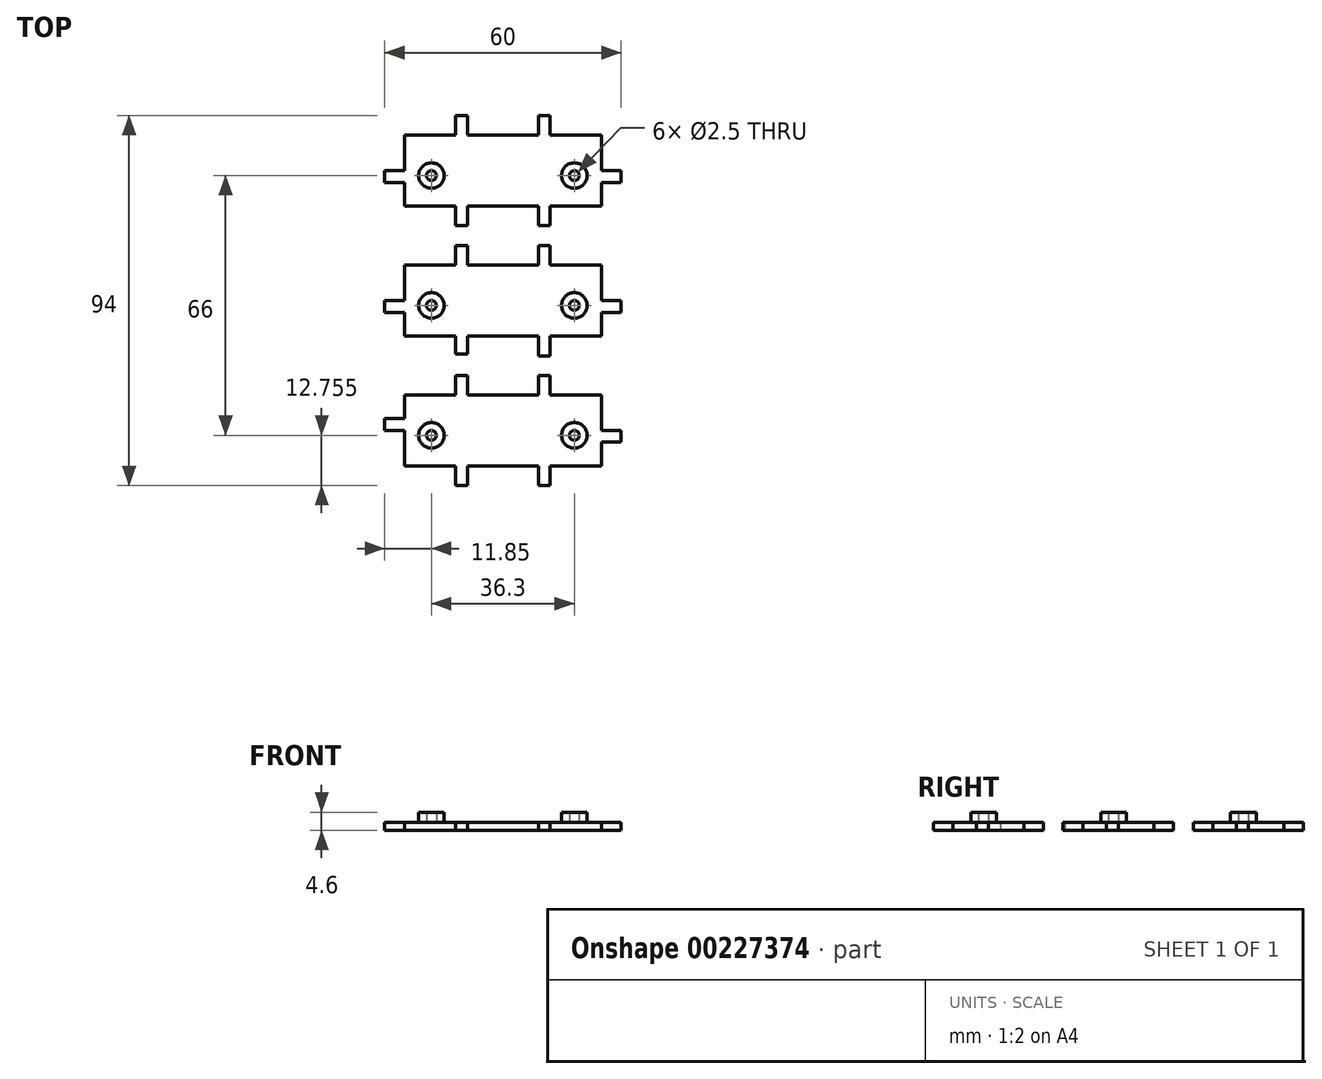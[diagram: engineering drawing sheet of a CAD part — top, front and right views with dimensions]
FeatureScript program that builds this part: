
annotation { "Feature Type Name" : "Feature", "Feature Type Description" : "" }
export const myFeature = defineFeature(function(context is Context, id is Id, definition is map)
    precondition{}
    {
        {
            var Q0;
            Q0=qCreatedBy(makeId("Top.planeOp"),FACE);
            var sketch = newSketch(context, id + "F0", { "sketchPlane" : qUnion([Q0])});
            skLineSegment(sketch, "E0.bottom", {"start": v(-14.26, 31.33) * mm, "end": v(35.74, 31.33) * mm});
            skLineSegment(sketch, "E0.top", {"start": v(-14.26, 13.33) * mm, "end": v(35.74, 13.33) * mm});
            skLineSegment(sketch, "E0.left", {"start": v(-14.26, 31.33) * mm, "end": v(-14.26, 13.33) * mm});
            skLineSegment(sketch, "E0.right", {"start": v(35.74, 31.33) * mm, "end": v(35.74, 13.33) * mm});
            skLineSegment(sketch, "E1.bottom", {"start": v(-14.26, -1.67) * mm, "end": v(35.74, -1.67) * mm});
            skLineSegment(sketch, "E1.top", {"start": v(-14.26, -19.67) * mm, "end": v(35.74, -19.67) * mm});
            skLineSegment(sketch, "E1.left", {"start": v(-14.26, -1.67) * mm, "end": v(-14.26, -19.67) * mm});
            skLineSegment(sketch, "E1.right", {"start": v(35.74, -1.67) * mm, "end": v(35.74, -19.67) * mm});
            skLineSegment(sketch, "E2.bottom", {"start": v(-14.26, -34.67) * mm, "end": v(35.74, -34.67) * mm});
            skLineSegment(sketch, "E2.top", {"start": v(-14.26, -52.67) * mm, "end": v(35.74, -52.67) * mm});
            skLineSegment(sketch, "E2.left", {"start": v(-14.26, -34.67) * mm, "end": v(-14.26, -52.67) * mm});
            skLineSegment(sketch, "E2.right", {"start": v(35.74, -34.67) * mm, "end": v(35.74, -52.67) * mm});
            skLineSegment(sketch, "E3.bottom", {"start": v(-1.26, 31.33) * mm, "end": v(1.74, 31.33) * mm});
            skLineSegment(sketch, "E3.top", {"start": v(-1.26, 36.33) * mm, "end": v(1.74, 36.33) * mm});
            skLineSegment(sketch, "E3.left", {"start": v(-1.26, 31.33) * mm, "end": v(-1.26, 36.33) * mm});
            skLineSegment(sketch, "E3.right", {"start": v(1.74, 31.33) * mm, "end": v(1.74, 36.33) * mm});
            skLineSegment(sketch, "E4.bottom", {"start": v(19.74, 36.33) * mm, "end": v(22.74, 36.33) * mm});
            skLineSegment(sketch, "E4.top", {"start": v(19.74, 31.33) * mm, "end": v(22.74, 31.33) * mm});
            skLineSegment(sketch, "E4.left", {"start": v(19.74, 36.33) * mm, "end": v(19.74, 31.33) * mm});
            skLineSegment(sketch, "E4.right", {"start": v(22.74, 36.33) * mm, "end": v(22.74, 31.33) * mm});
            skPoint(sketch, "E5.firstSnap0", {"position": v(-1.26, 33.83) * mm});
            skLineSegment(sketch, "E5.bottom", {"start": v(-1.26, 13.33) * mm, "end": v(1.74, 13.33) * mm});
            skLineSegment(sketch, "E5.top", {"start": v(-1.26, 8.33) * mm, "end": v(1.74, 8.33) * mm});
            skLineSegment(sketch, "E5.left", {"start": v(-1.26, 13.33) * mm, "end": v(-1.26, 8.33) * mm});
            skLineSegment(sketch, "E5.right", {"start": v(1.74, 13.33) * mm, "end": v(1.74, 8.33) * mm});
            skLineSegment(sketch, "E6.bottom", {"start": v(19.74, 13.33) * mm, "end": v(22.74, 13.33) * mm});
            skLineSegment(sketch, "E6.top", {"start": v(19.74, 8.33) * mm, "end": v(22.74, 8.33) * mm});
            skLineSegment(sketch, "E6.left", {"start": v(19.74, 13.33) * mm, "end": v(19.74, 8.33) * mm});
            skLineSegment(sketch, "E6.right", {"start": v(22.74, 13.33) * mm, "end": v(22.74, 8.33) * mm});
            skLineSegment(sketch, "E7.bottom", {"start": v(-1.26, -1.67) * mm, "end": v(1.74, -1.67) * mm});
            skLineSegment(sketch, "E7.top", {"start": v(-1.26, 3.33) * mm, "end": v(1.74, 3.33) * mm});
            skLineSegment(sketch, "E7.left", {"start": v(-1.26, -1.67) * mm, "end": v(-1.26, 3.33) * mm});
            skLineSegment(sketch, "E7.right", {"start": v(1.74, -1.67) * mm, "end": v(1.74, 3.33) * mm});
            skLineSegment(sketch, "E8.bottom", {"start": v(19.74, 3.33) * mm, "end": v(22.74, 3.33) * mm});
            skLineSegment(sketch, "E8.top", {"start": v(19.74, -1.67) * mm, "end": v(22.74, -1.67) * mm});
            skLineSegment(sketch, "E8.left", {"start": v(19.74, 3.33) * mm, "end": v(19.74, -1.67) * mm});
            skLineSegment(sketch, "E8.right", {"start": v(22.74, 3.33) * mm, "end": v(22.74, -1.67) * mm});
            skLineSegment(sketch, "E9.bottom", {"start": v(-1.26, -19.67) * mm, "end": v(1.74, -19.67) * mm});
            skLineSegment(sketch, "E9.top", {"start": v(-1.26, -24.3) * mm, "end": v(1.74, -24.3) * mm});
            skLineSegment(sketch, "E9.left", {"start": v(-1.26, -19.67) * mm, "end": v(-1.26, -24.3) * mm});
            skLineSegment(sketch, "E9.right", {"start": v(1.74, -19.67) * mm, "end": v(1.74, -24.3) * mm});
            skLineSegment(sketch, "E10.bottom", {"start": v(19.74, -19.67) * mm, "end": v(22.74, -19.67) * mm});
            skLineSegment(sketch, "E10.top", {"start": v(19.74, -24.78) * mm, "end": v(22.74, -24.78) * mm});
            skLineSegment(sketch, "E10.left", {"start": v(19.74, -19.67) * mm, "end": v(19.74, -24.78) * mm});
            skLineSegment(sketch, "E10.right", {"start": v(22.74, -19.67) * mm, "end": v(22.74, -24.78) * mm});
            skLineSegment(sketch, "E11.bottom", {"start": v(-1.26, -29.67) * mm, "end": v(1.74, -29.67) * mm});
            skLineSegment(sketch, "E11.top", {"start": v(-1.26, -34.67) * mm, "end": v(1.74, -34.67) * mm});
            skLineSegment(sketch, "E11.left", {"start": v(-1.26, -29.67) * mm, "end": v(-1.26, -34.67) * mm});
            skLineSegment(sketch, "E11.right", {"start": v(1.74, -29.67) * mm, "end": v(1.74, -34.67) * mm});
            skLineSegment(sketch, "E12.bottom", {"start": v(19.74, -29.67) * mm, "end": v(22.74, -29.67) * mm});
            skLineSegment(sketch, "E12.top", {"start": v(19.74, -34.67) * mm, "end": v(22.74, -34.67) * mm});
            skLineSegment(sketch, "E12.left", {"start": v(19.74, -29.67) * mm, "end": v(19.74, -34.67) * mm});
            skLineSegment(sketch, "E12.right", {"start": v(22.74, -29.67) * mm, "end": v(22.74, -34.67) * mm});
            skLineSegment(sketch, "E13.bottom", {"start": v(-1.26, -52.67) * mm, "end": v(1.74, -52.67) * mm});
            skLineSegment(sketch, "E13.top", {"start": v(-1.26, -57.67) * mm, "end": v(1.74, -57.67) * mm});
            skLineSegment(sketch, "E13.left", {"start": v(-1.26, -52.67) * mm, "end": v(-1.26, -57.67) * mm});
            skLineSegment(sketch, "E13.right", {"start": v(1.74, -52.67) * mm, "end": v(1.74, -57.67) * mm});
            skLineSegment(sketch, "E14.bottom", {"start": v(19.74, -52.67) * mm, "end": v(22.74, -52.67) * mm});
            skLineSegment(sketch, "E14.top", {"start": v(19.74, -57.67) * mm, "end": v(22.74, -57.67) * mm});
            skLineSegment(sketch, "E14.left", {"start": v(19.74, -52.67) * mm, "end": v(19.74, -57.67) * mm});
            skLineSegment(sketch, "E14.right", {"start": v(22.74, -52.67) * mm, "end": v(22.74, -57.67) * mm});
            skLineSegment(sketch, "E15.bottom", {"start": v(-14.26, 22.33) * mm, "end": v(-19.26, 22.33) * mm});
            skLineSegment(sketch, "E15.top", {"start": v(-14.26, 19.33) * mm, "end": v(-19.26, 19.33) * mm});
            skLineSegment(sketch, "E15.left", {"start": v(-14.26, 22.33) * mm, "end": v(-14.26, 19.33) * mm});
            skLineSegment(sketch, "E15.right", {"start": v(-19.26, 22.33) * mm, "end": v(-19.26, 19.33) * mm});
            skLineSegment(sketch, "E16.bottom", {"start": v(35.74, 22.33) * mm, "end": v(40.74, 22.33) * mm});
            skLineSegment(sketch, "E16.top", {"start": v(35.74, 19.33) * mm, "end": v(40.74, 19.33) * mm});
            skLineSegment(sketch, "E16.left", {"start": v(35.74, 22.33) * mm, "end": v(35.74, 19.33) * mm});
            skLineSegment(sketch, "E16.right", {"start": v(40.74, 22.33) * mm, "end": v(40.74, 19.33) * mm});
            skLineSegment(sketch, "E17.bottom", {"start": v(35.74, -10.67) * mm, "end": v(40.74, -10.67) * mm});
            skLineSegment(sketch, "E17.top", {"start": v(35.74, -13.67) * mm, "end": v(40.74, -13.67) * mm});
            skLineSegment(sketch, "E17.left", {"start": v(35.74, -10.67) * mm, "end": v(35.74, -13.67) * mm});
            skLineSegment(sketch, "E17.right", {"start": v(40.74, -10.67) * mm, "end": v(40.74, -13.67) * mm});
            skLineSegment(sketch, "E18.bottom", {"start": v(-14.26, -10.67) * mm, "end": v(-19.26, -10.67) * mm});
            skLineSegment(sketch, "E18.top", {"start": v(-14.26, -13.67) * mm, "end": v(-19.26, -13.67) * mm});
            skLineSegment(sketch, "E18.left", {"start": v(-14.26, -10.67) * mm, "end": v(-14.26, -13.67) * mm});
            skLineSegment(sketch, "E18.right", {"start": v(-19.26, -10.67) * mm, "end": v(-19.26, -13.67) * mm});
            skLineSegment(sketch, "E19.bottom", {"start": v(35.74, -43.67) * mm, "end": v(40.74, -43.67) * mm});
            skLineSegment(sketch, "E19.top", {"start": v(35.74, -46.67) * mm, "end": v(40.74, -46.67) * mm});
            skLineSegment(sketch, "E19.left", {"start": v(35.74, -43.67) * mm, "end": v(35.74, -46.67) * mm});
            skLineSegment(sketch, "E19.right", {"start": v(40.74, -43.67) * mm, "end": v(40.74, -46.67) * mm});
            skPoint(sketch, "E20.oppositeSnap0", {"position": v(-14.26, -43.67) * mm});
            skLineSegment(sketch, "E20.bottom", {"start": v(-14.26, -40.67) * mm, "end": v(-19.26, -40.67) * mm});
            skLineSegment(sketch, "E20.top", {"start": v(-14.26, -43.67) * mm, "end": v(-19.26, -43.67) * mm});
            skLineSegment(sketch, "E20.left", {"start": v(-14.26, -40.67) * mm, "end": v(-14.26, -43.67) * mm});
            skLineSegment(sketch, "E20.right", {"start": v(-19.26, -40.67) * mm, "end": v(-19.26, -43.67) * mm});
            skSolve(sketch);
        }
        {
            var Q0;
            Q0 = qSketchRegion(id + "F0", true);
            extrude(context, id + "F1", {"entities" : qUnion([Q0]), "depth" : 2 * mm});
        }
        {
            var Q0;
            Q0=makeQuery(id+"F1.opExtrude","CAP_FACE",FACE,{"disambiguationData":[OSD([sQuery(id+"F0.wireOp",EDGE,"E0.bottom"),sQuery(id+"F0.wireOp",EDGE,"E0.top"),sQuery(id+"F0.wireOp",EDGE,"E0.left"),sQuery(id+"F0.wireOp",EDGE,"E0.right"),sQuery(id+"F0.wireOp",EDGE,"E3.top"),sQuery(id+"F0.wireOp",EDGE,"E3.left"),sQuery(id+"F0.wireOp",EDGE,"E3.right"),sQuery(id+"F0.wireOp",EDGE,"2ueM8kfB-ZWXk-Q4G8-vLaj-rHVx2HCc8esA.bottom"),sQuery(id+"F0.wireOp",EDGE,"2ueM8kfB-ZWXk-Q4G8-vLaj-rHVx2HCc8esA.left"),sQuery(id+"F0.wireOp",EDGE,"2ueM8kfB-ZWXk-Q4G8-vLaj-rHVx2HCc8esA.right"),sQuery(id+"F0.wireOp",EDGE,"E4.bottom"),sQuery(id+"F0.wireOp",EDGE,"E4.left"),sQuery(id+"F0.wireOp",EDGE,"E4.right"),sQuery(id+"F0.wireOp",EDGE,"E5.top"),sQuery(id+"F0.wireOp",EDGE,"E5.left"),sQuery(id+"F0.wireOp",EDGE,"E5.right"),sQuery(id+"F0.wireOp",EDGE,"hTrA4h0s-yYhv-GkRn-lq8r-nXCzr6xYdK8y.top"),sQuery(id+"F0.wireOp",EDGE,"hTrA4h0s-yYhv-GkRn-lq8r-nXCzr6xYdK8y.left"),sQuery(id+"F0.wireOp",EDGE,"hTrA4h0s-yYhv-GkRn-lq8r-nXCzr6xYdK8y.right"),sQuery(id+"F0.wireOp",EDGE,"E6.top"),sQuery(id+"F0.wireOp",EDGE,"E6.left"),sQuery(id+"F0.wireOp",EDGE,"E6.right")])],"isStart":false});
            var sketch = newSketch(context, id + "F2", { "sketchPlane" : qUnion([Q0])});
            skCircle(sketch, "E21", {"center": v(-7.41, 21.08) * mm, "radius": 3.25 * mm});
            skCircle(sketch, "E22", {"center": v(28.89, 21.08) * mm, "radius": 3.25 * mm});
            skCircle(sketch, "E23", {"center": v(-7.41, -11.92) * mm, "radius": 3.25 * mm});
            skCircle(sketch, "E24", {"center": v(-7.41, -44.92) * mm, "radius": 3.25 * mm});
            skCircle(sketch, "E25", {"center": v(28.89, -11.92) * mm, "radius": 3.25 * mm});
            skCircle(sketch, "E26", {"center": v(28.89, -44.92) * mm, "radius": 3.25 * mm});
            skCircle(sketch, "E27", {"center": v(28.89, 21.08) * mm, "radius": 1.25 * mm});
            skCircle(sketch, "E28", {"center": v(-7.41, 21.08) * mm, "radius": 1.25 * mm});
            skCircle(sketch, "E29", {"center": v(28.89, -11.92) * mm, "radius": 1.25 * mm});
            skCircle(sketch, "E30", {"center": v(-7.41, -11.92) * mm, "radius": 1.25 * mm});
            skCircle(sketch, "E31", {"center": v(28.89, -44.92) * mm, "radius": 1.25 * mm});
            skCircle(sketch, "E32", {"center": v(-7.41, -44.92) * mm, "radius": 1.25 * mm});
            skSolve(sketch);
        }
        {
            var Q0;
            Q0 = qSketchRegion(id + "F2", true);
            extrude(context, id + "F3", {"entities" : qUnion([Q0]), "depth" : 2.6 * mm});
        }
    });
